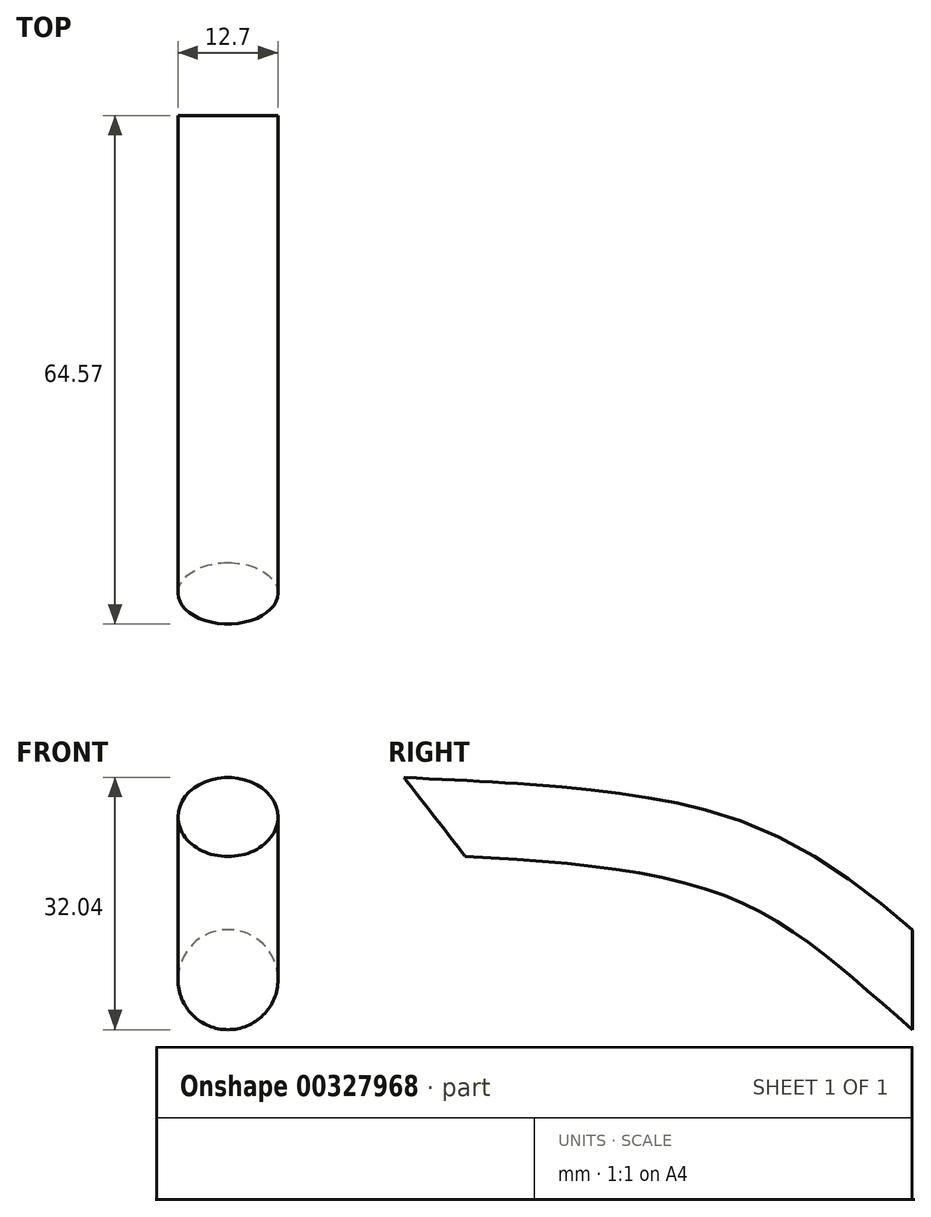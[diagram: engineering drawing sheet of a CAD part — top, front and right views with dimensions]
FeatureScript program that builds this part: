
annotation { "Feature Type Name" : "Feature", "Feature Type Description" : "" }
export const myFeature = defineFeature(function(context is Context, id is Id, definition is map)
    precondition{}
    {
        {
            var Q0;
            Q0=qCreatedBy(makeId("Right.planeOp"),FACE);
            var sketch = newSketch(context, id + "F0", { "sketchPlane" : qUnion([Q0])});
            skFitSpline(sketch, "E0", {"points": [v(0, 0) * mm, v(-22.45, 15.11) * mm, v(-60.67, 20.67) * mm], "startDerivative": vector(-44.5, 38.4) * mm, "endDerivative": vector(-75.93, 3.96) * mm});
            skSolve(sketch);
        }
        {
            var Q0;
            Q0=qCreatedBy(makeId("Front.planeOp"),FACE);
            var sketch = newSketch(context, id + "F1", { "sketchPlane" : qUnion([Q0])});
            skCircle(sketch, "E1", {"center": v(0, 0) * mm, "radius": 6.35 * mm});
            skSolve(sketch);
        }
        {
            var Q0;
            Q0=makeQuery(id+"F1.imprint","IMPRINT",FACE,{"disambiguationData":[TD([[makeQuery(id+"F1.imprint","IMPRINT",EDGE,{"derivedFrom":sQuery(id+"F1.wireOp",EDGE,"E1")}),1.0]])]});
            var Q1;
            Q1=sQuery(id+"F0.wireOp",EDGE,"E0");
            sweep(context, id + "F2", {"profiles" : qUnion([Q0]), "path" : qUnion([Q1])});
        }
    });
